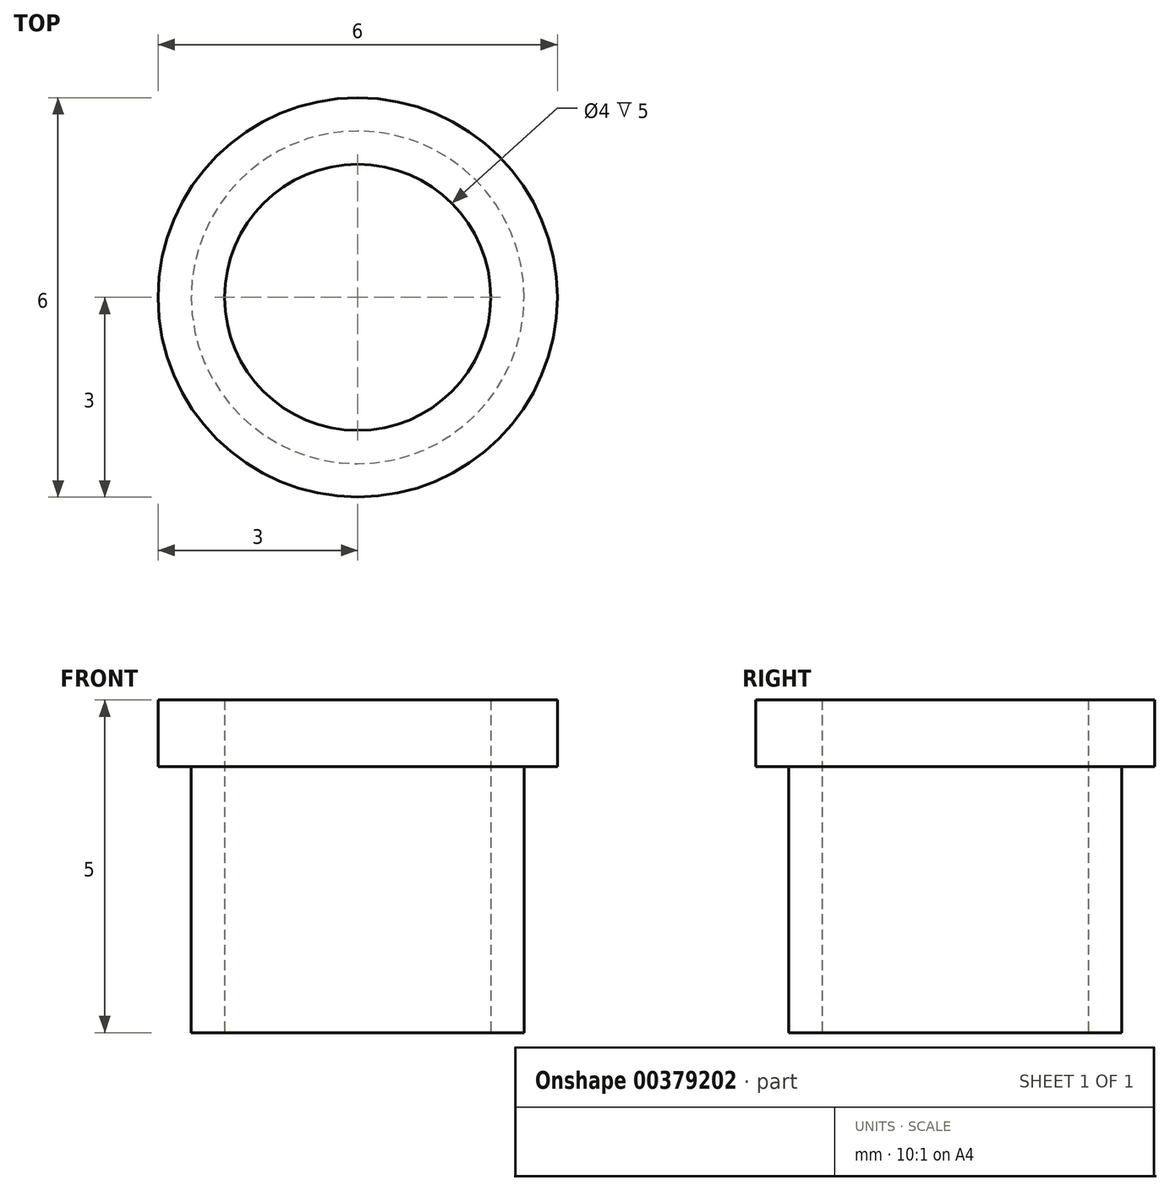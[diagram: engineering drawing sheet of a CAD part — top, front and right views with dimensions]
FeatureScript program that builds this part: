
annotation { "Feature Type Name" : "Feature", "Feature Type Description" : "" }
export const myFeature = defineFeature(function(context is Context, id is Id, definition is map)
    precondition{}
    {
        {
            var Q0;
            Q0=qCreatedBy(makeId("Top.planeOp"),FACE);
            var sketch = newSketch(context, id + "F0", { "sketchPlane" : qUnion([Q0])});
            skCircle(sketch, "E0", {"center": v(0, 0) * mm, "radius": 2.5 * mm});
            skCircle(sketch, "E1", {"center": v(0, 0) * mm, "radius": 2 * mm});
            skSolve(sketch);
        }
        {
            var Q0;
            Q0=makeQuery(id+"F0.imprint","IMPRINT",FACE,{"disambiguationData":[TD([[makeQuery(id+"F0.imprint","IMPRINT",EDGE,{"derivedFrom":sQuery(id+"F0.wireOp",EDGE,"E0")}),1.0]])]});
            extrude(context, id + "F1", {"entities" : qUnion([Q0]), "depth" : 5 * mm});
        }
        {
            var Q0;
            Q0=makeQuery(id+"F1.opExtrude","CAP_FACE",FACE,{"disambiguationData":[OSD([sQuery(id+"F0.wireOp",EDGE,"E0"),sQuery(id+"F0.wireOp",EDGE,"E1")])],"isStart":false});
            var sketch = newSketch(context, id + "F2", { "sketchPlane" : qUnion([Q0])});
            skCircle(sketch, "E2", {"center": v(0, 0) * mm, "radius": 3 * mm});
            skCircle(sketch, "E3", {"center": v(0, 0) * mm, "radius": 2 * mm});
            skSolve(sketch);
        }
        {
            var Q0;
            Q0=makeQuery(id+"F2.imprint","IMPRINT",FACE,{"disambiguationData":[TD([[makeQuery(id+"F2.imprint","IMPRINT",EDGE,{"derivedFrom":sQuery(id+"F2.wireOp",EDGE,"E2")}),1.0]])]});
            extrude(context, id + "F3", {"entities" : qUnion([Q0]), "operationType" : NewBodyOperationType.ADD, "oppositeDirection" : true, "depth" : 1 * mm});
        }
    });
